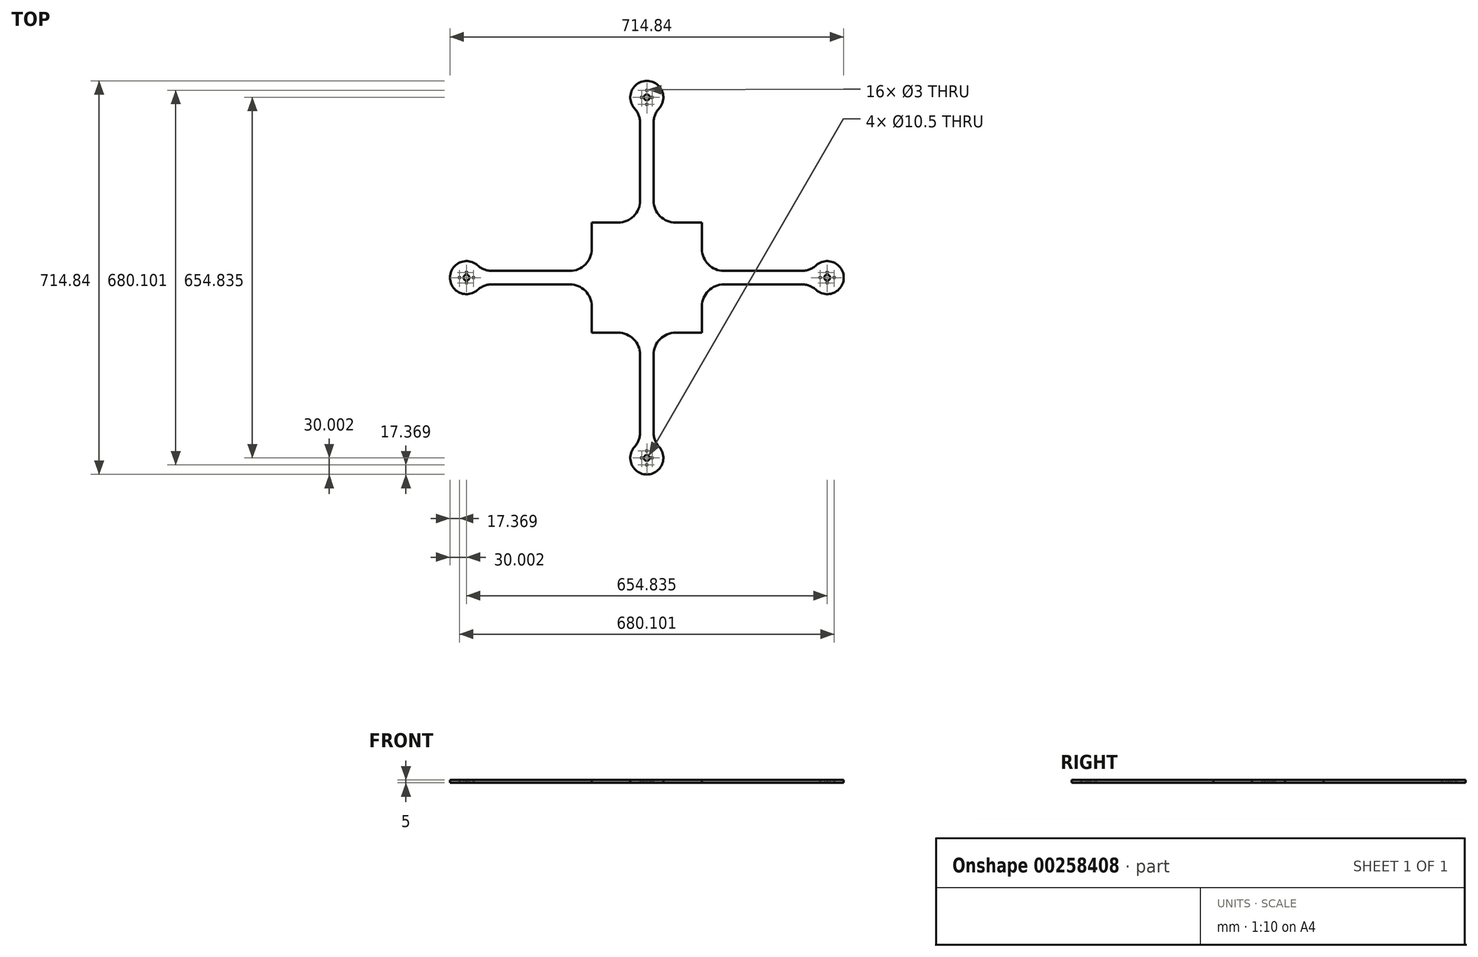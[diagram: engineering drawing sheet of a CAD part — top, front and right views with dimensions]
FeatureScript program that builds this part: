
annotation { "Feature Type Name" : "Feature", "Feature Type Description" : "" }
export const myFeature = defineFeature(function(context is Context, id is Id, definition is map)
    precondition{}
    {
        {
            var Q0;
            Q0=qCreatedBy(makeId("Top.planeOp"),FACE);
            var sketch = newSketch(context, id + "F0", { "sketchPlane" : qUnion([Q0])});
            skLineSegment(sketch, "E0.bottom", {"start": v(100, -100) * mm, "end": v(52.18, -100) * mm});
            skLineSegment(sketch, "E0.top", {"start": v(100, 100) * mm, "end": v(52.18, 100) * mm});
            skLineSegment(sketch, "E0.left", {"start": v(100, -100) * mm, "end": v(100, -52.18) * mm});
            skLineSegment(sketch, "E0.right", {"start": v(-100, -100) * mm, "end": v(-100, -52.18) * mm});
            skPoint(sketch, "E0.middle", {"position": v(0, 0) * mm});
            skLineSegment(sketch, "E1", {"start": v(-100, 0) * mm, "end": v(100, 0) * mm, "construction": true});
            skLineSegment(sketch, "E2", {"start": v(0, 100) * mm, "end": v(0, -100) * mm, "construction": true});
            skLineSegment(sketch, "E3", {"start": v(-12.18, 140) * mm, "end": v(-12.18, 280.75) * mm});
            skLineSegment(sketch, "E4.MirrorCS", {"start": v(12.18, 140) * mm, "end": v(12.18, 280.75) * mm});
            skLineSegment(sketch, "E5.trimOffspring", {"start": v(-52.18, 100) * mm, "end": v(-100, 100) * mm});
            skLineSegment(sketch, "E6", {"start": v(0, 100) * mm, "end": v(0, 427.92) * mm, "construction": true});
            skLineSegment(sketch, "E7", {"start": v(100, 100) * mm, "end": v(-100, -100) * mm, "construction": true});
            skLineSegment(sketch, "E8", {"start": v(-100, 100) * mm, "end": v(100, -100) * mm, "construction": true});
            skLineSegment(sketch, "E9.MirrorCS", {"start": v(140, 12.18) * mm, "end": v(280.75, 12.18) * mm});
            skLineSegment(sketch, "E10.MirrorCS", {"start": v(140, -12.18) * mm, "end": v(280.75, -12.18) * mm});
            skLineSegment(sketch, "E11.MirrorCS", {"start": v(-140, 12.18) * mm, "end": v(-280.75, 12.18) * mm});
            skLineSegment(sketch, "E12.MirrorCS", {"start": v(-140, -12.18) * mm, "end": v(-280.75, -12.18) * mm});
            skLineSegment(sketch, "E13.MirrorCS", {"start": v(-12.18, -140) * mm, "end": v(-12.18, -280.75) * mm});
            skLineSegment(sketch, "E14.MirrorCS", {"start": v(12.18, -140) * mm, "end": v(12.18, -280.75) * mm});
            skLineSegment(sketch, "E15.trimOffspring", {"start": v(100, 52.18) * mm, "end": v(100, 100) * mm});
            skLineSegment(sketch, "E16.trimOffspring", {"start": v(-52.18, -100) * mm, "end": v(-100, -100) * mm});
            skLineSegment(sketch, "E17.trimOffspring", {"start": v(-100, 52.18) * mm, "end": v(-100, 100) * mm});
            skArc(sketch, "E18", {"start": v(22.36, 307.42) * mm, "mid": v(0, 357.42) * mm, "end": v(-22.36, 307.42) * mm});
            skArc(sketch, "E19.MirrorCS", {"start": v(307.42, 22.36) * mm, "mid": v(357.42, 0) * mm, "end": v(307.42, -22.36) * mm});
            skArc(sketch, "E20.MirrorCS", {"start": v(-307.42, -22.36) * mm, "mid": v(-357.42, 0) * mm, "end": v(-307.42, 22.36) * mm});
            skArc(sketch, "E21.MirrorCS", {"start": v(-22.36, -307.42) * mm, "mid": v(0, -357.42) * mm, "end": v(22.36, -307.42) * mm});
            skPoint(sketch, "E22.visualSharp", {"position": v(-12.18, 300) * mm});
            skArc(sketch, "E22.filletArc", {"start": v(-12.18, 280.75) * mm, "mid": v(-14.8, 295.03) * mm, "end": v(-22.36, 307.42) * mm});
            skPoint(sketch, "E23.visualSharp", {"position": v(-12.18, 100) * mm});
            skArc(sketch, "E23.filletArc", {"start": v(-52.18, 100) * mm, "mid": v(-23.9, 111.72) * mm, "end": v(-12.18, 140) * mm});
            skPoint(sketch, "E24.visualSharp", {"position": v(12.18, 100) * mm});
            skArc(sketch, "E24.filletArc", {"start": v(12.18, 140) * mm, "mid": v(23.9, 111.72) * mm, "end": v(52.18, 100) * mm});
            skPoint(sketch, "E25.visualSharp", {"position": v(12.18, 300) * mm});
            skArc(sketch, "E25.filletArc", {"start": v(22.36, 307.42) * mm, "mid": v(14.8, 295.03) * mm, "end": v(12.18, 280.75) * mm});
            skPoint(sketch, "E26.visualSharp", {"position": v(100, 12.18) * mm});
            skArc(sketch, "E26.filletArc", {"start": v(100, 52.18) * mm, "mid": v(111.72, 23.9) * mm, "end": v(140, 12.18) * mm});
            skPoint(sketch, "E27.visualSharp", {"position": v(100, -12.18) * mm});
            skArc(sketch, "E27.filletArc", {"start": v(140, -12.18) * mm, "mid": v(111.72, -23.9) * mm, "end": v(100, -52.18) * mm});
            skPoint(sketch, "E28.visualSharp", {"position": v(300, -12.18) * mm});
            skArc(sketch, "E28.filletArc", {"start": v(307.42, -22.36) * mm, "mid": v(295.03, -14.8) * mm, "end": v(280.75, -12.18) * mm});
            skPoint(sketch, "E29.visualSharp", {"position": v(300, 12.18) * mm});
            skArc(sketch, "E29.filletArc", {"start": v(280.75, 12.18) * mm, "mid": v(295.03, 14.8) * mm, "end": v(307.42, 22.36) * mm});
            skPoint(sketch, "E30.visualSharp", {"position": v(12.18, -100) * mm});
            skArc(sketch, "E30.filletArc", {"start": v(52.18, -100) * mm, "mid": v(23.9, -111.72) * mm, "end": v(12.18, -140) * mm});
            skPoint(sketch, "E31.visualSharp", {"position": v(-12.18, -100) * mm});
            skArc(sketch, "E31.filletArc", {"start": v(-12.18, -140) * mm, "mid": v(-23.9, -111.72) * mm, "end": v(-52.18, -100) * mm});
            skPoint(sketch, "E32.visualSharp", {"position": v(-12.18, -300) * mm});
            skArc(sketch, "E32.filletArc", {"start": v(-22.36, -307.42) * mm, "mid": v(-14.8, -295.03) * mm, "end": v(-12.18, -280.75) * mm});
            skPoint(sketch, "E33.visualSharp", {"position": v(12.18, -300) * mm});
            skArc(sketch, "E33.filletArc", {"start": v(12.18, -280.75) * mm, "mid": v(14.8, -295.03) * mm, "end": v(22.36, -307.42) * mm});
            skPoint(sketch, "E34.visualSharp", {"position": v(-300, -12.18) * mm});
            skArc(sketch, "E34.filletArc", {"start": v(-280.75, -12.18) * mm, "mid": v(-295.03, -14.8) * mm, "end": v(-307.42, -22.36) * mm});
            skPoint(sketch, "E35.visualSharp", {"position": v(-300, 12.18) * mm});
            skArc(sketch, "E35.filletArc", {"start": v(-307.42, 22.36) * mm, "mid": v(-295.03, 14.8) * mm, "end": v(-280.75, 12.18) * mm});
            skPoint(sketch, "E36.visualSharp", {"position": v(-100, -12.18) * mm});
            skArc(sketch, "E36.filletArc", {"start": v(-100, -52.18) * mm, "mid": v(-111.72, -23.9) * mm, "end": v(-140, -12.18) * mm});
            skPoint(sketch, "E37.visualSharp", {"position": v(-100, 12.18) * mm});
            skArc(sketch, "E37.filletArc", {"start": v(-140, 12.18) * mm, "mid": v(-111.72, 23.9) * mm, "end": v(-100, 52.18) * mm});
            skCircle(sketch, "E38", {"center": v(-327.42, 0) * mm, "radius": 5.25 * mm});
            skCircle(sketch, "E39", {"center": v(-327.35, 9.48) * mm, "radius": 1.5 * mm});
            skCircle(sketch, "E40.MirrorC", {"center": v(-314.65, -0.02) * mm, "radius": 1.5 * mm});
            skCircle(sketch, "E41.MirrorC", {"center": v(-340.05, -0.02) * mm, "radius": 1.5 * mm});
            skCircle(sketch, "E42.MirrorC", {"center": v(-327.35, -9.52) * mm, "radius": 1.5 * mm});
            skLineSegment(sketch, "E43", {"start": v(-327.42, 30) * mm, "end": v(-327.42, -30) * mm, "construction": true});
            skLineSegment(sketch, "E44", {"start": v(-357.42, 0) * mm, "end": v(-100, 0) * mm, "construction": true});
            skCircle(sketch, "E45.MirrorC", {"center": v(0.02, 314.65) * mm, "radius": 1.5 * mm});
            skCircle(sketch, "E46.MirrorC", {"center": v(0, 327.42) * mm, "radius": 5.25 * mm});
            skCircle(sketch, "E47.MirrorC", {"center": v(-9.48, 327.35) * mm, "radius": 1.5 * mm});
            skCircle(sketch, "E48.MirrorC", {"center": v(0.02, 340.05) * mm, "radius": 1.5 * mm});
            skCircle(sketch, "E49.MirrorC", {"center": v(9.52, 327.35) * mm, "radius": 1.5 * mm});
            skCircle(sketch, "E50.MirrorC", {"center": v(314.65, 0.02) * mm, "radius": 1.5 * mm});
            skCircle(sketch, "E51.MirrorC", {"center": v(340.05, 0.02) * mm, "radius": 1.5 * mm});
            skCircle(sketch, "E52.MirrorC", {"center": v(327.42, 0) * mm, "radius": 5.25 * mm});
            skCircle(sketch, "E53.MirrorC", {"center": v(327.35, 9.52) * mm, "radius": 1.5 * mm});
            skCircle(sketch, "E54.MirrorC", {"center": v(327.35, -9.48) * mm, "radius": 1.5 * mm});
            skCircle(sketch, "E55.MirrorC", {"center": v(9.48, -327.35) * mm, "radius": 1.5 * mm});
            skCircle(sketch, "E56.MirrorC", {"center": v(-9.52, -327.35) * mm, "radius": 1.5 * mm});
            skCircle(sketch, "E57.MirrorC", {"center": v(-0.02, -314.65) * mm, "radius": 1.5 * mm});
            skCircle(sketch, "E58.MirrorC", {"center": v(-0.02, -340.05) * mm, "radius": 1.5 * mm});
            skCircle(sketch, "E59.MirrorC", {"center": v(0, -327.42) * mm, "radius": 5.25 * mm});
            skSolve(sketch);
        }
        {
            var Q0;
            Q0 = qSketchRegion(id + "F0", true);
            extrude(context, id + "F1", {"entities" : qUnion([Q0]), "depth" : 5 * mm});
        }
    });
